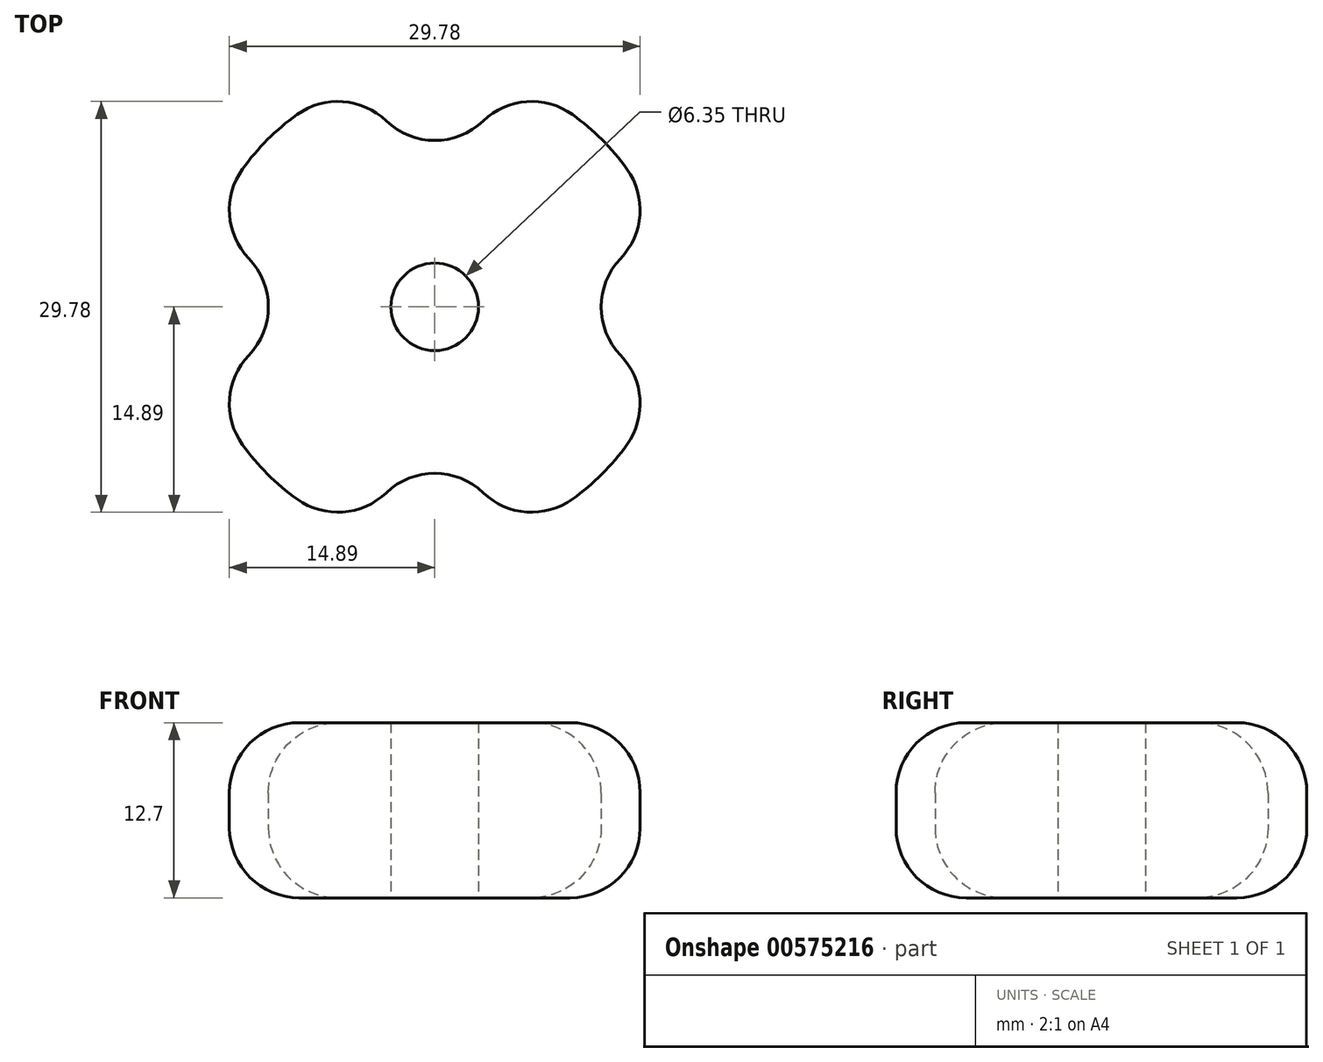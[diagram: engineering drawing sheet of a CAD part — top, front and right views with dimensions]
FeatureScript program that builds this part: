
annotation { "Feature Type Name" : "Feature", "Feature Type Description" : "" }
export const myFeature = defineFeature(function(context is Context, id is Id, definition is map)
    precondition{}
    {
        {
            var Q0;
            Q0=qCreatedBy(makeId("Top.planeOp"),FACE);
            var sketch = newSketch(context, id + "F0", { "sketchPlane" : qUnion([Q0])});
            skArc(sketch, "E0", {"start": v(5.02, -16.4) * mm, "mid": v(12.12, -12.12) * mm, "end": v(16.4, -5.02) * mm});
            skArc(sketch, "E1", {"start": v(-5.02, 16.4) * mm, "mid": v(0, 12.06) * mm, "end": v(5.02, 16.4) * mm});
            skCircle(sketch, "E2", {"center": v(0, 0) * mm, "radius": 22.23 * mm, "construction": true});
            skArc(sketch, "E3", {"start": v(-16.4, -5.02) * mm, "mid": v(-12.06, 0) * mm, "end": v(-16.4, 5.02) * mm});
            skArc(sketch, "E4", {"start": v(5.02, -16.4) * mm, "mid": v(0, -12.06) * mm, "end": v(-5.02, -16.4) * mm});
            skArc(sketch, "E5", {"start": v(16.4, 5.02) * mm, "mid": v(12.06, 0) * mm, "end": v(16.4, -5.02) * mm});
            skCircle(sketch, "E6", {"center": v(0, 0) * mm, "radius": 3.18 * mm});
            skArc(sketch, "E7.trimOffspring", {"start": v(16.4, 5.02) * mm, "mid": v(12.12, 12.12) * mm, "end": v(5.02, 16.4) * mm});
            skArc(sketch, "E8.trimOffspring", {"start": v(-5.02, 16.4) * mm, "mid": v(-12.12, 12.12) * mm, "end": v(-16.4, 5.02) * mm});
            skArc(sketch, "E9.trimOffspring", {"start": v(-16.4, -5.02) * mm, "mid": v(-12.12, -12.12) * mm, "end": v(-5.02, -16.4) * mm});
            skSolve(sketch);
        }
        {
            var Q0;
            Q0=qSketchRegion(id+"F0",true);
            extrude(context, id + "F1", {"entities" : qUnion([Q0]), "depth" : 12.7 * mm});
        }
        {
            var Q0;
            Q0=makeQuery(id+"F1.opExtrude","SWEPT_EDGE",EDGE,{"disambiguationData":[OSD([sQuery(id+"F0.wireOp",EDGE,"E1"),sQuery(id+"F0.wireOp",EDGE,"E7.trimOffspring")])]});
            var Q1;
            Q1=makeQuery(id+"F1.opExtrude","SWEPT_EDGE",EDGE,{"disambiguationData":[OSD([sQuery(id+"F0.wireOp",EDGE,"E1"),sQuery(id+"F0.wireOp",EDGE,"E8.trimOffspring")])]});
            var Q2;
            Q2=makeQuery(id+"F1.opExtrude","SWEPT_EDGE",EDGE,{"disambiguationData":[OSD([sQuery(id+"F0.wireOp",EDGE,"E5"),sQuery(id+"F0.wireOp",EDGE,"E7.trimOffspring")])]});
            var Q3;
            Q3=makeQuery(id+"F1.opExtrude","SWEPT_EDGE",EDGE,{"disambiguationData":[OSD([sQuery(id+"F0.wireOp",EDGE,"E0"),sQuery(id+"F0.wireOp",EDGE,"E5")])]});
            var Q4;
            Q4=makeQuery(id+"F1.opExtrude","SWEPT_EDGE",EDGE,{"disambiguationData":[OSD([sQuery(id+"F0.wireOp",EDGE,"E0"),sQuery(id+"F0.wireOp",EDGE,"E4")])]});
            var Q5;
            Q5=makeQuery(id+"F1.opExtrude","SWEPT_EDGE",EDGE,{"disambiguationData":[OSD([sQuery(id+"F0.wireOp",EDGE,"E4"),sQuery(id+"F0.wireOp",EDGE,"E9.trimOffspring")])]});
            var Q6;
            Q6=makeQuery(id+"F1.opExtrude","SWEPT_EDGE",EDGE,{"disambiguationData":[OSD([sQuery(id+"F0.wireOp",EDGE,"E3"),sQuery(id+"F0.wireOp",EDGE,"E9.trimOffspring")])]});
            var Q7;
            Q7=makeQuery(id+"F1.opExtrude","SWEPT_EDGE",EDGE,{"disambiguationData":[OSD([sQuery(id+"F0.wireOp",EDGE,"E3"),sQuery(id+"F0.wireOp",EDGE,"E8.trimOffspring")])]});
            fillet(context, id + "F2", {"entities" : qUnion([Q0, Q1, Q2, Q3, Q4, Q5, Q6, Q7]), "radius" : 5.08 * mm, "tangentPropagation" : true, "allowEdgeOverflow" : false});
        }
        {
            var Q0;
            {var subQ0=sQuery(id+"F0.wireOp",EDGE,"E9.trimOffspring");var subQ1=sQuery(id+"F0.wireOp",EDGE,"E4");Q0=makeQuery(id+"F2.opFillet","BLEND_EDGE",EDGE,{"blendedFrom":[makeQuery(id+"F1.opExtrude","SWEPT_EDGE",EDGE,{"disambiguationData":[OSD([subQ1,subQ0])]}),makeQuery(id+"F1.opExtrude","CAP_FACE",FACE,{"disambiguationData":[OSD([sQuery(id+"F0.wireOp",EDGE,"E0"),sQuery(id+"F0.wireOp",EDGE,"E1"),sQuery(id+"F0.wireOp",EDGE,"E3"),subQ1,sQuery(id+"F0.wireOp",EDGE,"E5"),sQuery(id+"F0.wireOp",EDGE,"E6"),sQuery(id+"F0.wireOp",EDGE,"E7.trimOffspring"),sQuery(id+"F0.wireOp",EDGE,"E8.trimOffspring"),subQ0])],"isStart":false})],"blendedInto":[makeQuery(id+"F1.opExtrude","CAP_FACE",FACE,{"disambiguationData":[OSD([sQuery(id+"F0.wireOp",EDGE,"E0"),sQuery(id+"F0.wireOp",EDGE,"E1"),sQuery(id+"F0.wireOp",EDGE,"E3"),subQ1,sQuery(id+"F0.wireOp",EDGE,"E5"),sQuery(id+"F0.wireOp",EDGE,"E6"),sQuery(id+"F0.wireOp",EDGE,"E7.trimOffspring"),sQuery(id+"F0.wireOp",EDGE,"E8.trimOffspring"),subQ0])],"isStart":false})]});}
            var Q1;
            Q1=makeQuery(id+"F1.opExtrude","CAP_EDGE",EDGE,{"disambiguationData":[OSD([sQuery(id+"F0.wireOp",EDGE,"E4")])],"isStart":false});
            var Q2;
            {var subQ0=sQuery(id+"F0.wireOp",EDGE,"E4");var subQ1=sQuery(id+"F0.wireOp",EDGE,"E0");Q2=makeQuery(id+"F2.opFillet","BLEND_EDGE",EDGE,{"blendedFrom":[makeQuery(id+"F1.opExtrude","SWEPT_EDGE",EDGE,{"disambiguationData":[OSD([subQ1,subQ0])]}),makeQuery(id+"F1.opExtrude","CAP_FACE",FACE,{"disambiguationData":[OSD([subQ1,sQuery(id+"F0.wireOp",EDGE,"E1"),sQuery(id+"F0.wireOp",EDGE,"E3"),subQ0,sQuery(id+"F0.wireOp",EDGE,"E5"),sQuery(id+"F0.wireOp",EDGE,"E6"),sQuery(id+"F0.wireOp",EDGE,"E7.trimOffspring"),sQuery(id+"F0.wireOp",EDGE,"E8.trimOffspring"),sQuery(id+"F0.wireOp",EDGE,"E9.trimOffspring")])],"isStart":false})],"blendedInto":[makeQuery(id+"F1.opExtrude","CAP_FACE",FACE,{"disambiguationData":[OSD([subQ1,sQuery(id+"F0.wireOp",EDGE,"E1"),sQuery(id+"F0.wireOp",EDGE,"E3"),subQ0,sQuery(id+"F0.wireOp",EDGE,"E5"),sQuery(id+"F0.wireOp",EDGE,"E6"),sQuery(id+"F0.wireOp",EDGE,"E7.trimOffspring"),sQuery(id+"F0.wireOp",EDGE,"E8.trimOffspring"),sQuery(id+"F0.wireOp",EDGE,"E9.trimOffspring")])],"isStart":false})]});}
            var Q3;
            Q3=makeQuery(id+"F1.opExtrude","CAP_EDGE",EDGE,{"disambiguationData":[OSD([sQuery(id+"F0.wireOp",EDGE,"E5")])],"isStart":false});
            var Q4;
            {var subQ0=sQuery(id+"F0.wireOp",EDGE,"E5");var subQ1=sQuery(id+"F0.wireOp",EDGE,"E0");Q4=makeQuery(id+"F2.opFillet","BLEND_EDGE",EDGE,{"blendedFrom":[makeQuery(id+"F1.opExtrude","SWEPT_EDGE",EDGE,{"disambiguationData":[OSD([subQ1,subQ0])]}),makeQuery(id+"F1.opExtrude","CAP_FACE",FACE,{"disambiguationData":[OSD([subQ1,sQuery(id+"F0.wireOp",EDGE,"E1"),sQuery(id+"F0.wireOp",EDGE,"E3"),sQuery(id+"F0.wireOp",EDGE,"E4"),subQ0,sQuery(id+"F0.wireOp",EDGE,"E6"),sQuery(id+"F0.wireOp",EDGE,"E7.trimOffspring"),sQuery(id+"F0.wireOp",EDGE,"E8.trimOffspring"),sQuery(id+"F0.wireOp",EDGE,"E9.trimOffspring")])],"isStart":false})],"blendedInto":[makeQuery(id+"F1.opExtrude","CAP_FACE",FACE,{"disambiguationData":[OSD([subQ1,sQuery(id+"F0.wireOp",EDGE,"E1"),sQuery(id+"F0.wireOp",EDGE,"E3"),sQuery(id+"F0.wireOp",EDGE,"E4"),subQ0,sQuery(id+"F0.wireOp",EDGE,"E6"),sQuery(id+"F0.wireOp",EDGE,"E7.trimOffspring"),sQuery(id+"F0.wireOp",EDGE,"E8.trimOffspring"),sQuery(id+"F0.wireOp",EDGE,"E9.trimOffspring")])],"isStart":false})]});}
            var Q5;
            {var subQ0=sQuery(id+"F0.wireOp",EDGE,"E7.trimOffspring");var subQ1=sQuery(id+"F0.wireOp",EDGE,"E1");Q5=makeQuery(id+"F2.opFillet","BLEND_EDGE",EDGE,{"blendedFrom":[makeQuery(id+"F1.opExtrude","SWEPT_EDGE",EDGE,{"disambiguationData":[OSD([subQ1,subQ0])]}),makeQuery(id+"F1.opExtrude","CAP_FACE",FACE,{"disambiguationData":[OSD([sQuery(id+"F0.wireOp",EDGE,"E0"),subQ1,sQuery(id+"F0.wireOp",EDGE,"E3"),sQuery(id+"F0.wireOp",EDGE,"E4"),sQuery(id+"F0.wireOp",EDGE,"E5"),sQuery(id+"F0.wireOp",EDGE,"E6"),subQ0,sQuery(id+"F0.wireOp",EDGE,"E8.trimOffspring"),sQuery(id+"F0.wireOp",EDGE,"E9.trimOffspring")])],"isStart":false})],"blendedInto":[makeQuery(id+"F1.opExtrude","CAP_FACE",FACE,{"disambiguationData":[OSD([sQuery(id+"F0.wireOp",EDGE,"E0"),subQ1,sQuery(id+"F0.wireOp",EDGE,"E3"),sQuery(id+"F0.wireOp",EDGE,"E4"),sQuery(id+"F0.wireOp",EDGE,"E5"),sQuery(id+"F0.wireOp",EDGE,"E6"),subQ0,sQuery(id+"F0.wireOp",EDGE,"E8.trimOffspring"),sQuery(id+"F0.wireOp",EDGE,"E9.trimOffspring")])],"isStart":false})]});}
            var Q6;
            Q6=makeQuery(id+"F1.opExtrude","CAP_EDGE",EDGE,{"disambiguationData":[OSD([sQuery(id+"F0.wireOp",EDGE,"E1")])],"isStart":false});
            var Q7;
            {var subQ0=sQuery(id+"F0.wireOp",EDGE,"E8.trimOffspring");var subQ1=sQuery(id+"F0.wireOp",EDGE,"E3");Q7=makeQuery(id+"F2.opFillet","BLEND_EDGE",EDGE,{"blendedFrom":[makeQuery(id+"F1.opExtrude","SWEPT_EDGE",EDGE,{"disambiguationData":[OSD([subQ1,subQ0])]}),makeQuery(id+"F1.opExtrude","CAP_FACE",FACE,{"disambiguationData":[OSD([sQuery(id+"F0.wireOp",EDGE,"E0"),sQuery(id+"F0.wireOp",EDGE,"E1"),subQ1,sQuery(id+"F0.wireOp",EDGE,"E4"),sQuery(id+"F0.wireOp",EDGE,"E5"),sQuery(id+"F0.wireOp",EDGE,"E6"),sQuery(id+"F0.wireOp",EDGE,"E7.trimOffspring"),subQ0,sQuery(id+"F0.wireOp",EDGE,"E9.trimOffspring")])],"isStart":false})],"blendedInto":[makeQuery(id+"F1.opExtrude","CAP_FACE",FACE,{"disambiguationData":[OSD([sQuery(id+"F0.wireOp",EDGE,"E0"),sQuery(id+"F0.wireOp",EDGE,"E1"),subQ1,sQuery(id+"F0.wireOp",EDGE,"E4"),sQuery(id+"F0.wireOp",EDGE,"E5"),sQuery(id+"F0.wireOp",EDGE,"E6"),sQuery(id+"F0.wireOp",EDGE,"E7.trimOffspring"),subQ0,sQuery(id+"F0.wireOp",EDGE,"E9.trimOffspring")])],"isStart":false})]});}
            var Q8;
            {var subQ0=sQuery(id+"F0.wireOp",EDGE,"E8.trimOffspring");var subQ1=sQuery(id+"F0.wireOp",EDGE,"E1");Q8=makeQuery(id+"F2.opFillet","BLEND_EDGE",EDGE,{"blendedFrom":[makeQuery(id+"F1.opExtrude","SWEPT_EDGE",EDGE,{"disambiguationData":[OSD([subQ1,subQ0])]}),makeQuery(id+"F1.opExtrude","CAP_FACE",FACE,{"disambiguationData":[OSD([sQuery(id+"F0.wireOp",EDGE,"E0"),subQ1,sQuery(id+"F0.wireOp",EDGE,"E3"),sQuery(id+"F0.wireOp",EDGE,"E4"),sQuery(id+"F0.wireOp",EDGE,"E5"),sQuery(id+"F0.wireOp",EDGE,"E6"),sQuery(id+"F0.wireOp",EDGE,"E7.trimOffspring"),subQ0,sQuery(id+"F0.wireOp",EDGE,"E9.trimOffspring")])],"isStart":false})],"blendedInto":[makeQuery(id+"F1.opExtrude","CAP_FACE",FACE,{"disambiguationData":[OSD([sQuery(id+"F0.wireOp",EDGE,"E0"),subQ1,sQuery(id+"F0.wireOp",EDGE,"E3"),sQuery(id+"F0.wireOp",EDGE,"E4"),sQuery(id+"F0.wireOp",EDGE,"E5"),sQuery(id+"F0.wireOp",EDGE,"E6"),sQuery(id+"F0.wireOp",EDGE,"E7.trimOffspring"),subQ0,sQuery(id+"F0.wireOp",EDGE,"E9.trimOffspring")])],"isStart":false})]});}
            var Q9;
            Q9=makeQuery(id+"F1.opExtrude","CAP_EDGE",EDGE,{"disambiguationData":[OSD([sQuery(id+"F0.wireOp",EDGE,"E4")])],"isStart":true});
            var Q10;
            {var subQ0=sQuery(id+"F0.wireOp",EDGE,"E9.trimOffspring");var subQ1=sQuery(id+"F0.wireOp",EDGE,"E4");Q10=makeQuery(id+"F2.opFillet","BLEND_EDGE",EDGE,{"blendedFrom":[makeQuery(id+"F1.opExtrude","SWEPT_EDGE",EDGE,{"disambiguationData":[OSD([subQ1,subQ0])]}),makeQuery(id+"F1.opExtrude","CAP_FACE",FACE,{"disambiguationData":[OSD([sQuery(id+"F0.wireOp",EDGE,"E0"),sQuery(id+"F0.wireOp",EDGE,"E1"),sQuery(id+"F0.wireOp",EDGE,"E3"),subQ1,sQuery(id+"F0.wireOp",EDGE,"E5"),sQuery(id+"F0.wireOp",EDGE,"E6"),sQuery(id+"F0.wireOp",EDGE,"E7.trimOffspring"),sQuery(id+"F0.wireOp",EDGE,"E8.trimOffspring"),subQ0])],"isStart":true})],"blendedInto":[makeQuery(id+"F1.opExtrude","CAP_FACE",FACE,{"disambiguationData":[OSD([sQuery(id+"F0.wireOp",EDGE,"E0"),sQuery(id+"F0.wireOp",EDGE,"E1"),sQuery(id+"F0.wireOp",EDGE,"E3"),subQ1,sQuery(id+"F0.wireOp",EDGE,"E5"),sQuery(id+"F0.wireOp",EDGE,"E6"),sQuery(id+"F0.wireOp",EDGE,"E7.trimOffspring"),sQuery(id+"F0.wireOp",EDGE,"E8.trimOffspring"),subQ0])],"isStart":true})]});}
            var Q11;
            {var subQ0=sQuery(id+"F0.wireOp",EDGE,"E4");var subQ1=sQuery(id+"F0.wireOp",EDGE,"E0");Q11=makeQuery(id+"F2.opFillet","BLEND_EDGE",EDGE,{"blendedFrom":[makeQuery(id+"F1.opExtrude","SWEPT_EDGE",EDGE,{"disambiguationData":[OSD([subQ1,subQ0])]}),makeQuery(id+"F1.opExtrude","CAP_FACE",FACE,{"disambiguationData":[OSD([subQ1,sQuery(id+"F0.wireOp",EDGE,"E1"),sQuery(id+"F0.wireOp",EDGE,"E3"),subQ0,sQuery(id+"F0.wireOp",EDGE,"E5"),sQuery(id+"F0.wireOp",EDGE,"E6"),sQuery(id+"F0.wireOp",EDGE,"E7.trimOffspring"),sQuery(id+"F0.wireOp",EDGE,"E8.trimOffspring"),sQuery(id+"F0.wireOp",EDGE,"E9.trimOffspring")])],"isStart":true})],"blendedInto":[makeQuery(id+"F1.opExtrude","CAP_FACE",FACE,{"disambiguationData":[OSD([subQ1,sQuery(id+"F0.wireOp",EDGE,"E1"),sQuery(id+"F0.wireOp",EDGE,"E3"),subQ0,sQuery(id+"F0.wireOp",EDGE,"E5"),sQuery(id+"F0.wireOp",EDGE,"E6"),sQuery(id+"F0.wireOp",EDGE,"E7.trimOffspring"),sQuery(id+"F0.wireOp",EDGE,"E8.trimOffspring"),sQuery(id+"F0.wireOp",EDGE,"E9.trimOffspring")])],"isStart":true})]});}
            var Q12;
            {var subQ0=sQuery(id+"F0.wireOp",EDGE,"E5");var subQ1=sQuery(id+"F0.wireOp",EDGE,"E0");Q12=makeQuery(id+"F2.opFillet","BLEND_EDGE",EDGE,{"blendedFrom":[makeQuery(id+"F1.opExtrude","SWEPT_EDGE",EDGE,{"disambiguationData":[OSD([subQ1,subQ0])]}),makeQuery(id+"F1.opExtrude","CAP_FACE",FACE,{"disambiguationData":[OSD([subQ1,sQuery(id+"F0.wireOp",EDGE,"E1"),sQuery(id+"F0.wireOp",EDGE,"E3"),sQuery(id+"F0.wireOp",EDGE,"E4"),subQ0,sQuery(id+"F0.wireOp",EDGE,"E6"),sQuery(id+"F0.wireOp",EDGE,"E7.trimOffspring"),sQuery(id+"F0.wireOp",EDGE,"E8.trimOffspring"),sQuery(id+"F0.wireOp",EDGE,"E9.trimOffspring")])],"isStart":true})],"blendedInto":[makeQuery(id+"F1.opExtrude","CAP_FACE",FACE,{"disambiguationData":[OSD([subQ1,sQuery(id+"F0.wireOp",EDGE,"E1"),sQuery(id+"F0.wireOp",EDGE,"E3"),sQuery(id+"F0.wireOp",EDGE,"E4"),subQ0,sQuery(id+"F0.wireOp",EDGE,"E6"),sQuery(id+"F0.wireOp",EDGE,"E7.trimOffspring"),sQuery(id+"F0.wireOp",EDGE,"E8.trimOffspring"),sQuery(id+"F0.wireOp",EDGE,"E9.trimOffspring")])],"isStart":true})]});}
            var Q13;
            Q13=makeQuery(id+"F1.opExtrude","CAP_EDGE",EDGE,{"disambiguationData":[OSD([sQuery(id+"F0.wireOp",EDGE,"E5")])],"isStart":true});
            var Q14;
            {var subQ0=sQuery(id+"F0.wireOp",EDGE,"E7.trimOffspring");var subQ1=sQuery(id+"F0.wireOp",EDGE,"E5");Q14=makeQuery(id+"F2.opFillet","BLEND_EDGE",EDGE,{"blendedFrom":[makeQuery(id+"F1.opExtrude","SWEPT_EDGE",EDGE,{"disambiguationData":[OSD([subQ1,subQ0])]}),makeQuery(id+"F1.opExtrude","CAP_FACE",FACE,{"disambiguationData":[OSD([sQuery(id+"F0.wireOp",EDGE,"E0"),sQuery(id+"F0.wireOp",EDGE,"E1"),sQuery(id+"F0.wireOp",EDGE,"E3"),sQuery(id+"F0.wireOp",EDGE,"E4"),subQ1,sQuery(id+"F0.wireOp",EDGE,"E6"),subQ0,sQuery(id+"F0.wireOp",EDGE,"E8.trimOffspring"),sQuery(id+"F0.wireOp",EDGE,"E9.trimOffspring")])],"isStart":true})],"blendedInto":[makeQuery(id+"F1.opExtrude","CAP_FACE",FACE,{"disambiguationData":[OSD([sQuery(id+"F0.wireOp",EDGE,"E0"),sQuery(id+"F0.wireOp",EDGE,"E1"),sQuery(id+"F0.wireOp",EDGE,"E3"),sQuery(id+"F0.wireOp",EDGE,"E4"),subQ1,sQuery(id+"F0.wireOp",EDGE,"E6"),subQ0,sQuery(id+"F0.wireOp",EDGE,"E8.trimOffspring"),sQuery(id+"F0.wireOp",EDGE,"E9.trimOffspring")])],"isStart":true})]});}
            var Q15;
            {var subQ0=sQuery(id+"F0.wireOp",EDGE,"E9.trimOffspring");var subQ1=sQuery(id+"F0.wireOp",EDGE,"E3");Q15=makeQuery(id+"F2.opFillet","BLEND_EDGE",EDGE,{"blendedFrom":[makeQuery(id+"F1.opExtrude","SWEPT_EDGE",EDGE,{"disambiguationData":[OSD([subQ1,subQ0])]}),makeQuery(id+"F1.opExtrude","CAP_FACE",FACE,{"disambiguationData":[OSD([sQuery(id+"F0.wireOp",EDGE,"E0"),sQuery(id+"F0.wireOp",EDGE,"E1"),subQ1,sQuery(id+"F0.wireOp",EDGE,"E4"),sQuery(id+"F0.wireOp",EDGE,"E5"),sQuery(id+"F0.wireOp",EDGE,"E6"),sQuery(id+"F0.wireOp",EDGE,"E7.trimOffspring"),sQuery(id+"F0.wireOp",EDGE,"E8.trimOffspring"),subQ0])],"isStart":true})],"blendedInto":[makeQuery(id+"F1.opExtrude","CAP_FACE",FACE,{"disambiguationData":[OSD([sQuery(id+"F0.wireOp",EDGE,"E0"),sQuery(id+"F0.wireOp",EDGE,"E1"),subQ1,sQuery(id+"F0.wireOp",EDGE,"E4"),sQuery(id+"F0.wireOp",EDGE,"E5"),sQuery(id+"F0.wireOp",EDGE,"E6"),sQuery(id+"F0.wireOp",EDGE,"E7.trimOffspring"),sQuery(id+"F0.wireOp",EDGE,"E8.trimOffspring"),subQ0])],"isStart":true})]});}
            var Q16;
            Q16=makeQuery(id+"F1.opExtrude","CAP_EDGE",EDGE,{"disambiguationData":[OSD([sQuery(id+"F0.wireOp",EDGE,"E3")])],"isStart":true});
            var Q17;
            {var subQ0=sQuery(id+"F0.wireOp",EDGE,"E8.trimOffspring");var subQ1=sQuery(id+"F0.wireOp",EDGE,"E3");Q17=makeQuery(id+"F2.opFillet","BLEND_EDGE",EDGE,{"blendedFrom":[makeQuery(id+"F1.opExtrude","SWEPT_EDGE",EDGE,{"disambiguationData":[OSD([subQ1,subQ0])]}),makeQuery(id+"F1.opExtrude","CAP_FACE",FACE,{"disambiguationData":[OSD([sQuery(id+"F0.wireOp",EDGE,"E0"),sQuery(id+"F0.wireOp",EDGE,"E1"),subQ1,sQuery(id+"F0.wireOp",EDGE,"E4"),sQuery(id+"F0.wireOp",EDGE,"E5"),sQuery(id+"F0.wireOp",EDGE,"E6"),sQuery(id+"F0.wireOp",EDGE,"E7.trimOffspring"),subQ0,sQuery(id+"F0.wireOp",EDGE,"E9.trimOffspring")])],"isStart":true})],"blendedInto":[makeQuery(id+"F1.opExtrude","CAP_FACE",FACE,{"disambiguationData":[OSD([sQuery(id+"F0.wireOp",EDGE,"E0"),sQuery(id+"F0.wireOp",EDGE,"E1"),subQ1,sQuery(id+"F0.wireOp",EDGE,"E4"),sQuery(id+"F0.wireOp",EDGE,"E5"),sQuery(id+"F0.wireOp",EDGE,"E6"),sQuery(id+"F0.wireOp",EDGE,"E7.trimOffspring"),subQ0,sQuery(id+"F0.wireOp",EDGE,"E9.trimOffspring")])],"isStart":true})]});}
            var Q18;
            {var subQ0=sQuery(id+"F0.wireOp",EDGE,"E8.trimOffspring");var subQ1=sQuery(id+"F0.wireOp",EDGE,"E1");Q18=makeQuery(id+"F2.opFillet","BLEND_EDGE",EDGE,{"blendedFrom":[makeQuery(id+"F1.opExtrude","SWEPT_EDGE",EDGE,{"disambiguationData":[OSD([subQ1,subQ0])]}),makeQuery(id+"F1.opExtrude","CAP_FACE",FACE,{"disambiguationData":[OSD([sQuery(id+"F0.wireOp",EDGE,"E0"),subQ1,sQuery(id+"F0.wireOp",EDGE,"E3"),sQuery(id+"F0.wireOp",EDGE,"E4"),sQuery(id+"F0.wireOp",EDGE,"E5"),sQuery(id+"F0.wireOp",EDGE,"E6"),sQuery(id+"F0.wireOp",EDGE,"E7.trimOffspring"),subQ0,sQuery(id+"F0.wireOp",EDGE,"E9.trimOffspring")])],"isStart":true})],"blendedInto":[makeQuery(id+"F1.opExtrude","CAP_FACE",FACE,{"disambiguationData":[OSD([sQuery(id+"F0.wireOp",EDGE,"E0"),subQ1,sQuery(id+"F0.wireOp",EDGE,"E3"),sQuery(id+"F0.wireOp",EDGE,"E4"),sQuery(id+"F0.wireOp",EDGE,"E5"),sQuery(id+"F0.wireOp",EDGE,"E6"),sQuery(id+"F0.wireOp",EDGE,"E7.trimOffspring"),subQ0,sQuery(id+"F0.wireOp",EDGE,"E9.trimOffspring")])],"isStart":true})]});}
            var Q19;
            Q19=makeQuery(id+"F1.opExtrude","CAP_EDGE",EDGE,{"disambiguationData":[OSD([sQuery(id+"F0.wireOp",EDGE,"E1")])],"isStart":true});
            fillet(context, id + "F3", {"entities" : qUnion([Q0, Q1, Q2, Q3, Q4, Q5, Q6, Q7, Q8, Q9, Q10, Q11, Q12, Q13, Q14, Q15, Q16, Q17, Q18, Q19]), "radius" : 5.08 * mm, "tangentPropagation" : true, "allowEdgeOverflow" : false});
        }
    });
